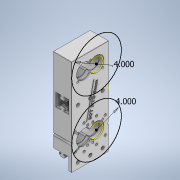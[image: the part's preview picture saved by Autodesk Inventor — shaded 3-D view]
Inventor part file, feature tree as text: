
AUTODESK INVENTOR PART (.ipt)
format: ipt  version: 2020 (Build 240168000, 168)  size: 855,552 bytes
history: native  units: in
note: dims shown in document units (in); Inventor stores cm internally (conversion verified against a paired STEP export)
features: reference x24, extrude x10, sketch x10, other x4, chamfer x1, fillet x1
ambient origin geometry x8: Origin, YZ Plane, XZ Plane, XY Plane, X Axis, Y Axis, Z Axis, Center Point
bodies: Solid1 (feature_tree)
feature tree (50):
  extrude  "Extrusion1"  Depth=5.0in
  extrude  "Extrusion2"  Depth=3.0in TaperAngle=0.0deg
  extrude  "Extrusion4"  TaperAngle=0.0deg  [1 undecoded]
  extrude  "Extrusion5"  Depth=1.126in
  extrude  "Extrusion6"  Depth=1.226in
  extrude  "Extrusion7"  Depth=1.126in
  extrude  "Extrusion8"  Depth=1.226in
  chamfer  "Chamfer3"  Distance=0.064in
  extrude  "Extrusion9"  Depth=0.165in
  fillet  "Fillet1"  [1 undecoded]
  sketch  "Sketch13"  dims[d50=1.4291in d51=0.165in d52=0.0in d53=0.0in]
  extrude  "Extrusion11"  Depth=1.0in
  extrude  "Extrusion12"  Depth=3.1496in TaperAngle=360.0deg
  reference  "Reference1"
  reference  "Reference2"
  reference  "Reference3"
  reference  "Reference4"
  reference  "Reference5"
  reference  "Reference6"
  reference  "Reference7"
  reference  "Reference8"
  reference  "Reference9"
  reference  "Reference10"
  reference  "Reference11"
  reference  "Reference12"
  reference  "Reference13"
  reference  "Reference14"
  reference  "Reference15"
  reference  "Reference16"
  reference  "Reference17"
  reference  "Reference18"
  reference  "Reference19"
  reference  "Reference20"
  reference  "Reference21"
  reference  "Reference22"
  reference  "Reference23"
  reference  "Reference24"
  sketch  "Sketch2"  dims[d0=1.5in d1=5.0in]
  sketch  "Sketch4"  dims[d2=0.2461in d3=3.0in d4=0.0in]
  sketch  "Sketch5"  dims[d7=0.2656in d24=0.0in d25=0.0in]
  sketch  "Sketch6"  dims[d31=1.023in d32=1.126in]
  sketch  "Sketch7"  dims[d33=0.314in d34=0.0in d35=1.226in]
  sketch  "Sketch8"  dims[d36=0.064in d37=0.0in d41=1.126in]
  sketch  "Sketch9"  dims[d42=0.314in d43=0.0in d44=1.226in d45=0.064in d46=0.0in]
  sketch  "Sketch14"  dims[d54=0.025in d55=0.125in d56=45.0deg d57=1.0in]
  sketch  "Sketch15"  dims[d58=0.196in d59=3.1496in d61=360.0deg d63=0.0in d64=0.0in d76=0.25in d77=2.75in d78=0.5in d79=0.5in d80=0.7874in d82=4.0in d83=1.1811in d85=1.0in d89=1.0in d90=2.0in d93=4.7254in d94=1.0in d95=1.0in d96=3.1496in d98=360.0deg d100=0.125in d101=4.0in d102=4.0in d103=0.05in d104=1.0in d105=1.0in d106=0.05in d107=0.0in d108=0.1in d109=0.05in d110=0.0in]
  other  "<userpath>\Documents\FRC\2020\ShooterPrototype.iam"
  other  "ShooterPrototype.iam"
  other  "9inSpacer:1"
  other  "1003-48-CL:4"
note: 2 required parameter values undecoded (feature->parameter linkage not recoverable at this tier; creation-order binding heuristic only, values carry confidence <= 0.55)
